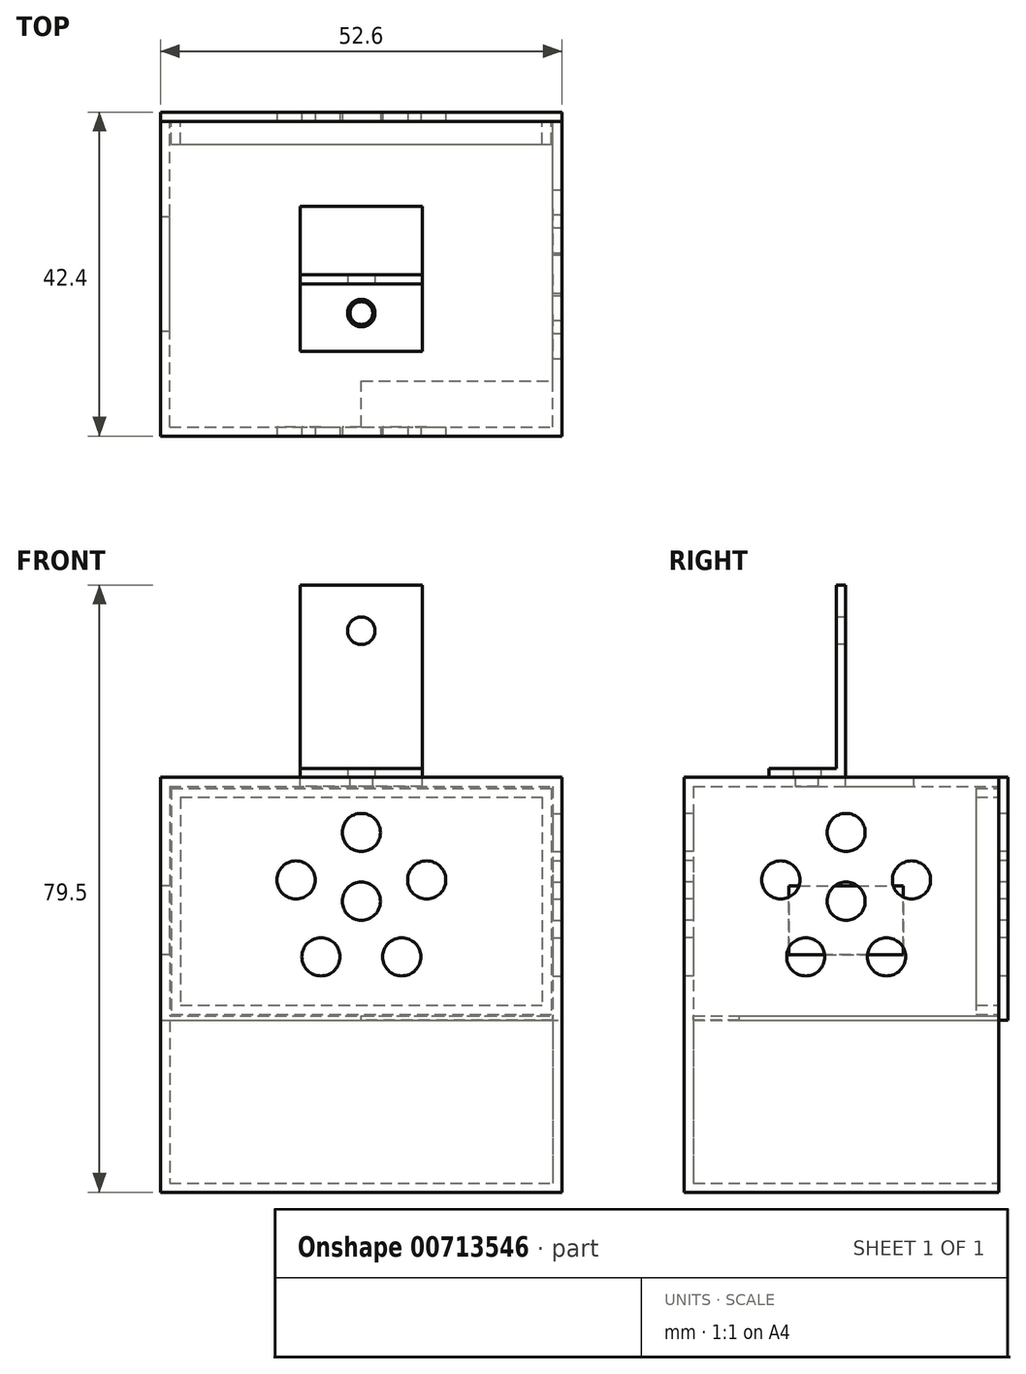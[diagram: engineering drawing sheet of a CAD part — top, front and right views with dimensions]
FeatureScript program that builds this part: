
annotation { "Feature Type Name" : "Feature", "Feature Type Description" : "" }
export const myFeature = defineFeature(function(context is Context, id is Id, definition is map)
    precondition{}
    {
        {
            var Q0;
            Q0=qCreatedBy(makeId("Top.planeOp"),FACE);
            var sketch = newSketch(context, id + "F0", { "sketchPlane" : qUnion([Q0])});
            skLineSegment(sketch, "E0.bottom", {"start": v(0, 0) * mm, "end": v(50.2, 0) * mm});
            skLineSegment(sketch, "E0.top", {"start": v(0, 40) * mm, "end": v(50.2, 40) * mm});
            skLineSegment(sketch, "E0.left", {"start": v(0, 0) * mm, "end": v(0, 40) * mm});
            skLineSegment(sketch, "E0.right", {"start": v(50.2, 0) * mm, "end": v(50.2, 40) * mm});
            skLineSegment(sketch, "E1.0", {"start": v(-1.2, -1.2) * mm, "end": v(-1.2, 40) * mm});
            skLineSegment(sketch, "E1.1", {"start": v(-1.2, -1.2) * mm, "end": v(51.4, -1.2) * mm});
            skLineSegment(sketch, "E1.2", {"start": v(51.4, -1.2) * mm, "end": v(51.4, 40) * mm});
            skLineSegment(sketch, "E2", {"start": v(-1.2, 40) * mm, "end": v(0, 40) * mm});
            skLineSegment(sketch, "E3", {"start": v(51.4, 40) * mm, "end": v(50.2, 40) * mm});
            skSolve(sketch);
        }
        {
            var Q0;
            Q0=makeQuery(id+"F0.imprint","IMPRINT",FACE,{"disambiguationData":[TD([[makeQuery(id+"F0.imprint","IMPRINT",EDGE,{"derivedFrom":sQuery(id+"F0.wireOp",EDGE,"E0.bottom")}),1.0]])]});
            extrude(context, id + "F1", {"entities" : qUnion([Q0]), "depth" : 1.2 * mm, "offsetDistance" : 25 * mm});
        }
        {
            var Q0;
            Q0=makeQuery(id+"F0.imprint","IMPRINT",FACE,{"disambiguationData":[TD([[makeQuery(id+"F0.imprint","IMPRINT",EDGE,{"derivedFrom":sQuery(id+"F0.wireOp",EDGE,"E0.bottom")}),-1.0]])]});
            extrude(context, id + "F2", {"entities" : qUnion([Q0]), "operationType" : NewBodyOperationType.ADD, "depth" : 22.5 * mm, "offsetDistance" : 25 * mm});
        }
        {
            var Q0;
            Q0=makeQuery(id+"F2.opExtrude","CAP_FACE",FACE,{"disambiguationData":[OSD([sQuery(id+"F0.wireOp",EDGE,"E0.bottom"),sQuery(id+"F0.wireOp",EDGE,"E0.left"),sQuery(id+"F0.wireOp",EDGE,"E0.right"),sQuery(id+"F0.wireOp",EDGE,"E1.0"),sQuery(id+"F0.wireOp",EDGE,"E1.1"),sQuery(id+"F0.wireOp",EDGE,"E1.2"),sQuery(id+"F0.wireOp",EDGE,"E2"),sQuery(id+"F0.wireOp",EDGE,"E3")])],"isStart":false});
            var sketch = newSketch(context, id + "F3", { "sketchPlane" : qUnion([Q0])});
            skLineSegment(sketch, "E4.0", {"start": v(0, 0) * mm, "end": v(0, 40) * mm});
            skLineSegment(sketch, "E4.1", {"start": v(-1.2, -1.2) * mm, "end": v(-1.2, 40) * mm});
            skLineSegment(sketch, "E4.2", {"start": v(-1.2, 40) * mm, "end": v(0, 40) * mm});
            skLineSegment(sketch, "E4.3", {"start": v(-1.2, -1.2) * mm, "end": v(51.4, -1.2) * mm});
            skLineSegment(sketch, "E4.4", {"start": v(51.4, -1.2) * mm, "end": v(51.4, 40) * mm});
            skLineSegment(sketch, "E4.5", {"start": v(51.4, 40) * mm, "end": v(50.2, 40) * mm});
            skLineSegment(sketch, "E5.bottom", {"start": v(-1.2, 40) * mm, "end": v(51.4, 40) * mm});
            skLineSegment(sketch, "E5.left", {"start": v(-1.2, 40) * mm, "end": v(-1.2, -1.2) * mm});
            skLineSegment(sketch, "E5.right", {"start": v(51.4, 40) * mm, "end": v(51.4, -1.2) * mm});
            skSolve(sketch);
        }
        {
            var Q0;
            {var subQ0=sQuery(id+"F3.wireOp",EDGE,"E4.0");Q0=makeQuery(id+"F3.imprint","IMPRINT",FACE,{"disambiguationData":[TD([[makeQuery(id+"F3.imprint","IMPRINT",EDGE,{"derivedFrom":subQ0}),-1.0]])]});}
            var Q1;
            {var subQ3=sQuery(id+"F3.wireOp",EDGE,"E4.0");Q1=makeQuery(id+"F3.imprint","IMPRINT",FACE,{"disambiguationData":[TD([[makeQuery(id+"F3.imprint","IMPRINT",EDGE,{"derivedFrom":subQ3}),1.0]])]});}
            extrude(context, id + "F4", {"entities" : qUnion([Q0, Q1]), "operationType" : NewBodyOperationType.ADD, "depth" : 0.6 * mm, "offsetDistance" : 25 * mm});
        }
        {
            var Q0;
            Q0=makeQuery(id+"F4.opExtrude","CAP_FACE",FACE,{"disambiguationData":[OSD([sQuery(id+"F3.wireOp",EDGE,"E5.bottom"),sQuery(id+"F3.wireOp",EDGE,"E4.3"),sQuery(id+"F3.wireOp",EDGE,"E5.left"),sQuery(id+"F3.wireOp",EDGE,"E5.right")])],"isStart":false});
            var sketch = newSketch(context, id + "F5", { "sketchPlane" : qUnion([Q0])});
            skLineSegment(sketch, "E6.0", {"start": v(-1.2, -1.2) * mm, "end": v(51.4, -1.2) * mm});
            skLineSegment(sketch, "E6.1", {"start": v(51.4, -1.2) * mm, "end": v(51.4, 40) * mm});
            skLineSegment(sketch, "E6.2", {"start": v(-1.2, -1.2) * mm, "end": v(-1.2, 40) * mm});
            skLineSegment(sketch, "E6.3", {"start": v(-1.2, 40) * mm, "end": v(51.4, 40) * mm});
            skLineSegment(sketch, "E7.0", {"start": v(0, 0) * mm, "end": v(50.2, 0) * mm});
            skLineSegment(sketch, "E7.1", {"start": v(50.2, 0) * mm, "end": v(50.2, 40) * mm});
            skLineSegment(sketch, "E7.2", {"start": v(0, 0) * mm, "end": v(0, 40) * mm});
            skPoint(sketch, "E8", {"position": v(25.1, 0) * mm});
            skLineSegment(sketch, "E9", {"start": v(25.1, 0) * mm, "end": v(25.1, 6) * mm});
            skLineSegment(sketch, "E10", {"start": v(25.1, 6) * mm, "end": v(50.2, 6) * mm});
            skSolve(sketch);
        }
        {
            var Q0;
            {var subQ3=sQuery(id+"F5.wireOp",EDGE,"E9");Q0=makeQuery(id+"F5.imprint","IMPRINT",FACE,{"disambiguationData":[TD([[makeQuery(id+"F5.imprint","IMPRINT",EDGE,{"derivedFrom":subQ3}),-1.0]])]});}
            extrude(context, id + "F6", {"entities" : qUnion([Q0]), "operationType" : NewBodyOperationType.REMOVE, "endBound" : BoundingType.UP_TO_NEXT, "oppositeDirection" : true, "depth" : 25 * mm, "offsetDistance" : 25 * mm});
        }
        {
            var Q0;
            Q0=makeQuery(id+"F4.opExtrude","CAP_FACE",FACE,{"disambiguationData":[OSD([sQuery(id+"F3.wireOp",EDGE,"E5.bottom"),sQuery(id+"F3.wireOp",EDGE,"E4.3"),sQuery(id+"F3.wireOp",EDGE,"E5.left"),sQuery(id+"F3.wireOp",EDGE,"E5.right")])],"isStart":false});
            var sketch = newSketch(context, id + "F7", { "sketchPlane" : qUnion([Q0])});
            skLineSegment(sketch, "E11.0", {"start": v(-1.2, -1.2) * mm, "end": v(-1.2, 40) * mm});
            skLineSegment(sketch, "E11.1", {"start": v(0, 0) * mm, "end": v(0, 40) * mm});
            skLineSegment(sketch, "E11.2", {"start": v(-1.2, -1.2) * mm, "end": v(51.4, -1.2) * mm});
            skLineSegment(sketch, "E11.3", {"start": v(0, 0) * mm, "end": v(50.2, 0) * mm});
            skLineSegment(sketch, "E11.4", {"start": v(50.2, 0) * mm, "end": v(50.2, 40) * mm});
            skSolve(sketch);
        }
        {
            var Q0;
            {var subQ3=sQuery(id+"F7.wireOp",EDGE,"E11.0");Q0=makeQuery(id+"F7.imprint","IMPRINT",FACE,{"disambiguationData":[TD([[makeQuery(id+"F7.imprint","IMPRINT",EDGE,{"derivedFrom":subQ3}),-1.0]])]});}
            extrude(context, id + "F8", {"entities" : qUnion([Q0]), "operationType" : NewBodyOperationType.ADD, "depth" : 30 * mm, "offsetDistance" : 25 * mm});
        }
        {
            var Q0;
            Q0=makeQuery(id+"F8.opExtrude","CAP_FACE",FACE,{"disambiguationData":[OSD([sQuery(id+"F3.wireOp",EDGE,"E5.bottom"),sQuery(id+"F3.wireOp",EDGE,"E5.right"),sQuery(id+"F7.wireOp",EDGE,"E11.0"),sQuery(id+"F7.wireOp",EDGE,"E11.1"),sQuery(id+"F7.wireOp",EDGE,"E11.2"),sQuery(id+"F7.wireOp",EDGE,"E11.3"),sQuery(id+"F7.wireOp",EDGE,"E11.4")])],"isStart":false});
            var sketch = newSketch(context, id + "F9", { "sketchPlane" : qUnion([Q0])});
            skLineSegment(sketch, "E12.0", {"start": v(51.4, -1.2) * mm, "end": v(51.4, 40) * mm});
            skLineSegment(sketch, "E12.1", {"start": v(50.2, 0) * mm, "end": v(50.2, 40) * mm});
            skLineSegment(sketch, "E12.2", {"start": v(0, 0) * mm, "end": v(50.2, 0) * mm});
            skLineSegment(sketch, "E12.3", {"start": v(-1.2, -1.2) * mm, "end": v(51.4, -1.2) * mm});
            skLineSegment(sketch, "E12.4", {"start": v(-1.2, -1.2) * mm, "end": v(-1.2, 40) * mm});
            skLineSegment(sketch, "E12.5", {"start": v(0, 0) * mm, "end": v(0, 40) * mm});
            skLineSegment(sketch, "E12.6", {"start": v(-1.2, 40) * mm, "end": v(0, 40) * mm});
            skLineSegment(sketch, "E12.7", {"start": v(50.2, 40) * mm, "end": v(51.4, 40) * mm});
            skLineSegment(sketch, "E13.bottom", {"start": v(-1.2, 40) * mm, "end": v(51.4, 40) * mm});
            skLineSegment(sketch, "E13.left", {"start": v(-1.2, 40) * mm, "end": v(-1.2, -1.2) * mm});
            skLineSegment(sketch, "E13.right", {"start": v(51.4, 40) * mm, "end": v(51.4, -1.2) * mm});
            skSolve(sketch);
        }
        {
            var Q0;
            {var subQ0=sQuery(id+"F9.wireOp",EDGE,"E12.1");Q0=makeQuery(id+"F9.imprint","IMPRINT",FACE,{"disambiguationData":[TD([[makeQuery(id+"F9.imprint","IMPRINT",EDGE,{"derivedFrom":subQ0}),1.0]])]});}
            var Q1;
            {var subQ3=sQuery(id+"F9.wireOp",EDGE,"E12.1");Q1=makeQuery(id+"F9.imprint","IMPRINT",FACE,{"disambiguationData":[TD([[makeQuery(id+"F9.imprint","IMPRINT",EDGE,{"derivedFrom":subQ3}),-1.0]])]});}
            extrude(context, id + "F10", {"entities" : qUnion([Q0, Q1]), "operationType" : NewBodyOperationType.ADD, "depth" : 1.2 * mm, "offsetDistance" : 25 * mm});
        }
        {
            var Q0;
            Q0=makeQuery(id+"F10.opExtrude","CAP_FACE",FACE,{"disambiguationData":[OSD([sQuery(id+"F9.wireOp",EDGE,"E13.bottom"),sQuery(id+"F9.wireOp",EDGE,"E12.3"),sQuery(id+"F9.wireOp",EDGE,"E13.left"),sQuery(id+"F9.wireOp",EDGE,"E13.right")])],"isStart":false});
            var sketch = newSketch(context, id + "F11", { "sketchPlane" : qUnion([Q0])});
            skLineSegment(sketch, "E14.bottom", {"start": v(17.1, 28.9) * mm, "end": v(33.1, 28.9) * mm});
            skLineSegment(sketch, "E14.top", {"start": v(17.1, 19.9) * mm, "end": v(33.1, 19.9) * mm});
            skLineSegment(sketch, "E14.left", {"start": v(17.1, 28.9) * mm, "end": v(17.1, 19.9) * mm});
            skLineSegment(sketch, "E14.right", {"start": v(33.1, 28.9) * mm, "end": v(33.1, 19.9) * mm});
            skLineSegment(sketch, "E15.0", {"start": v(51.4, -1.2) * mm, "end": v(51.4, 40) * mm});
            skLineSegment(sketch, "E15.1", {"start": v(-1.2, -1.2) * mm, "end": v(-1.2, 40) * mm});
            skLineSegment(sketch, "E15.2", {"start": v(-1.2, -1.2) * mm, "end": v(51.4, -1.2) * mm});
            skLineSegment(sketch, "E15.3", {"start": v(-1.2, 40) * mm, "end": v(51.4, 40) * mm});
            skPoint(sketch, "E16", {"position": v(25.1, 19.9) * mm});
            skCircle(sketch, "E17", {"center": v(25.1, 14.9) * mm, "radius": 1.5 * mm});
            skSolve(sketch);
        }
        {
            var Q0;
            Q0=makeQuery(id+"F11.imprint","IMPRINT",FACE,{"disambiguationData":[TD([[makeQuery(id+"F11.imprint","IMPRINT",EDGE,{"derivedFrom":sQuery(id+"F11.wireOp",EDGE,"E14.bottom")}),-1.0]])]});
            var Q1;
            Q1=makeQuery(id+"F11.imprint","IMPRINT",FACE,{"disambiguationData":[TD([[makeQuery(id+"F11.imprint","IMPRINT",EDGE,{"derivedFrom":sQuery(id+"F11.wireOp",EDGE,"E17")}),1.0]])]});
            extrude(context, id + "F12", {"entities" : qUnion([Q0, Q1]), "operationType" : NewBodyOperationType.REMOVE, "endBound" : BoundingType.UP_TO_NEXT, "oppositeDirection" : true, "depth" : 25 * mm, "offsetDistance" : 25 * mm});
        }
        {
            var Q0;
            Q0=makeQuery(id+"F10.boolean.opBoolean","MERGE",FACE,{"derivedFrom":[makeQuery(id+"F8.boolean.opBoolean","MERGE",FACE,{"derivedFrom":[makeQuery(id+"F4.boolean.opBoolean","MERGE",FACE,{"derivedFrom":[makeQuery(id+"F2.opExtrude","SWEPT_FACE",FACE,{"disambiguationData":[OSD([sQuery(id+"F0.wireOp",EDGE,"E1.0")])]}),makeQuery(id+"F4.opExtrude","SWEPT_FACE",FACE,{"disambiguationData":[OSD([sQuery(id+"F3.wireOp",EDGE,"E5.left")])]})]}),makeQuery(id+"F8.opExtrude","SWEPT_FACE",FACE,{"disambiguationData":[OSD([sQuery(id+"F7.wireOp",EDGE,"E11.0")])]})]}),makeQuery(id+"F10.opExtrude","SWEPT_FACE",FACE,{"disambiguationData":[OSD([sQuery(id+"F9.wireOp",EDGE,"E13.left")])]})]});
            var sketch = newSketch(context, id + "F13", { "sketchPlane" : qUnion([Q0])});
            skLineSegment(sketch, "E18.0", {"start": v(1.2, 54.3) * mm, "end": v(1.2, 0) * mm});
            skLineSegment(sketch, "E18.1", {"start": v(1.2, 54.3) * mm, "end": v(-40, 54.3) * mm});
            skLineSegment(sketch, "E18.2", {"start": v(-40, 54.3) * mm, "end": v(-40, 0) * mm});
            skLineSegment(sketch, "E18.3", {"start": v(1.2, 0) * mm, "end": v(-40, 0) * mm});
            skLineSegment(sketch, "E19.0", {"start": v(0, 23.1) * mm, "end": v(-40, 23.1) * mm});
            skLineSegment(sketch, "E20.1", {"start": v(0, 53.1) * mm, "end": v(-40, 53.1) * mm});
            skLineSegment(sketch, "E21.1", {"start": v(0, 53.1) * mm, "end": v(0, 23.1) * mm});
            skLineSegment(sketch, "E22.bottom", {"start": v(-27.5, 40.1) * mm, "end": v(-12.5, 40.1) * mm});
            skLineSegment(sketch, "E22.top", {"start": v(-27.5, 31.1) * mm, "end": v(-12.5, 31.1) * mm});
            skLineSegment(sketch, "E22.left", {"start": v(-27.5, 40.1) * mm, "end": v(-27.5, 31.1) * mm});
            skLineSegment(sketch, "E22.right", {"start": v(-12.5, 40.1) * mm, "end": v(-12.5, 31.1) * mm});
            skSolve(sketch);
        }
        {
            var Q0;
            Q0=makeQuery(id+"F13.imprint","IMPRINT",FACE,{"disambiguationData":[TD([[makeQuery(id+"F13.imprint","IMPRINT",EDGE,{"derivedFrom":sQuery(id+"F13.wireOp",EDGE,"E22.bottom")}),-1.0]])]});
            extrude(context, id + "F14", {"entities" : qUnion([Q0]), "operationType" : NewBodyOperationType.REMOVE, "endBound" : BoundingType.UP_TO_NEXT, "oppositeDirection" : true, "depth" : 25 * mm, "offsetDistance" : 25 * mm});
        }
        {
            var Q0;
            {var subQ0=sQuery(id+"F3.wireOp",EDGE,"E5.right");Q0=makeQuery(id+"F10.boolean.opBoolean","MERGE",FACE,{"derivedFrom":[makeQuery(id+"F8.boolean.opBoolean","MERGE",FACE,{"derivedFrom":[makeQuery(id+"F4.boolean.opBoolean","MERGE",FACE,{"derivedFrom":[makeQuery(id+"F2.opExtrude","SWEPT_FACE",FACE,{"disambiguationData":[OSD([sQuery(id+"F0.wireOp",EDGE,"E1.2")])]}),makeQuery(id+"F4.opExtrude","SWEPT_FACE",FACE,{"disambiguationData":[OSD([subQ0])]})]}),makeQuery(id+"F8.opExtrude","SWEPT_FACE",FACE,{"disambiguationData":[OSD([subQ0])]})]}),makeQuery(id+"F10.opExtrude","SWEPT_FACE",FACE,{"disambiguationData":[OSD([sQuery(id+"F9.wireOp",EDGE,"E13.right")])]})]});}
            var sketch = newSketch(context, id + "F15", { "sketchPlane" : qUnion([Q0])});
            skLineSegment(sketch, "E23.0", {"start": v(-1.2, 54.3) * mm, "end": v(40, 54.3) * mm});
            skLineSegment(sketch, "E23.1", {"start": v(40, 54.3) * mm, "end": v(40, 0) * mm});
            skLineSegment(sketch, "E23.2", {"start": v(-1.2, 54.3) * mm, "end": v(-1.2, 0) * mm});
            skLineSegment(sketch, "E23.3", {"start": v(-1.2, 0) * mm, "end": v(40, 0) * mm});
            skLineSegment(sketch, "E23.4", {"start": v(0, 53.1) * mm, "end": v(0, 1.2) * mm});
            skLineSegment(sketch, "E23.5", {"start": v(0, 53.1) * mm, "end": v(40, 53.1) * mm});
            skLineSegment(sketch, "E24.0", {"start": v(0, 1.2) * mm, "end": v(40, 1.2) * mm});
            skLineSegment(sketch, "E25.0", {"start": v(6, 23.1) * mm, "end": v(40, 23.1) * mm});
            skPoint(sketch, "E26", {"position": v(20, 53.1) * mm});
            skLineSegment(sketch, "E27", {"start": v(20, 53.1) * mm, "end": v(20, 23.1) * mm, "construction": true});
            skCircle(sketch, "E28", {"center": v(20, 38.1) * mm, "radius": 2.5 * mm});
            skCircle(sketch, "E29", {"center": v(20, 47.1) * mm, "radius": 2.5 * mm});
            skCircle(sketch, "E30.1.0", {"center": v(11.44, 40.88) * mm, "radius": 2.5 * mm});
            skCircle(sketch, "E30.2.0", {"center": v(14.7, 30.82) * mm, "radius": 2.5 * mm});
            skCircle(sketch, "E30.3.0", {"center": v(25.3, 30.82) * mm, "radius": 2.5 * mm});
            skCircle(sketch, "E30.4.0", {"center": v(28.56, 40.88) * mm, "radius": 2.5 * mm});
            skSolve(sketch);
        }
        {
            var Q0;
            Q0=makeQuery(id+"F15.imprint","IMPRINT",FACE,{"disambiguationData":[TD([[makeQuery(id+"F15.imprint","IMPRINT",EDGE,{"derivedFrom":sQuery(id+"F15.wireOp",EDGE,"E30.4.0")}),1.0]])]});
            var Q1;
            Q1=makeQuery(id+"F15.imprint","IMPRINT",FACE,{"disambiguationData":[TD([[makeQuery(id+"F15.imprint","IMPRINT",EDGE,{"derivedFrom":sQuery(id+"F15.wireOp",EDGE,"E29")}),1.0]])]});
            var Q2;
            Q2=makeQuery(id+"F15.imprint","IMPRINT",FACE,{"disambiguationData":[TD([[makeQuery(id+"F15.imprint","IMPRINT",EDGE,{"derivedFrom":sQuery(id+"F15.wireOp",EDGE,"E28")}),1.0]])]});
            var Q3;
            Q3=makeQuery(id+"F15.imprint","IMPRINT",FACE,{"disambiguationData":[TD([[makeQuery(id+"F15.imprint","IMPRINT",EDGE,{"derivedFrom":sQuery(id+"F15.wireOp",EDGE,"E30.1.0")}),1.0]])]});
            var Q4;
            Q4=makeQuery(id+"F15.imprint","IMPRINT",FACE,{"disambiguationData":[TD([[makeQuery(id+"F15.imprint","IMPRINT",EDGE,{"derivedFrom":sQuery(id+"F15.wireOp",EDGE,"E30.2.0")}),1.0]])]});
            var Q5;
            Q5=makeQuery(id+"F15.imprint","IMPRINT",FACE,{"disambiguationData":[TD([[makeQuery(id+"F15.imprint","IMPRINT",EDGE,{"derivedFrom":sQuery(id+"F15.wireOp",EDGE,"E30.3.0")}),1.0]])]});
            extrude(context, id + "F16", {"entities" : qUnion([Q0, Q1, Q2, Q3, Q4, Q5]), "operationType" : NewBodyOperationType.REMOVE, "endBound" : BoundingType.UP_TO_NEXT, "oppositeDirection" : true, "depth" : 25 * mm, "offsetDistance" : 25 * mm});
        }
        {
            var Q0;
            Q0=makeQuery(id+"F10.boolean.opBoolean","MERGE",FACE,{"derivedFrom":[makeQuery(id+"F8.boolean.opBoolean","MERGE",FACE,{"derivedFrom":[makeQuery(id+"F4.boolean.opBoolean","MERGE",FACE,{"derivedFrom":[makeQuery(id+"F2.opExtrude","SWEPT_FACE",FACE,{"disambiguationData":[OSD([sQuery(id+"F0.wireOp",EDGE,"E1.1")])]}),makeQuery(id+"F4.opExtrude","SWEPT_FACE",FACE,{"disambiguationData":[OSD([sQuery(id+"F3.wireOp",EDGE,"E4.3")])]})]}),makeQuery(id+"F8.opExtrude","SWEPT_FACE",FACE,{"disambiguationData":[OSD([sQuery(id+"F7.wireOp",EDGE,"E11.2")])]})]}),makeQuery(id+"F10.opExtrude","SWEPT_FACE",FACE,{"disambiguationData":[OSD([sQuery(id+"F9.wireOp",EDGE,"E12.3")])]})]});
            var sketch = newSketch(context, id + "F17", { "sketchPlane" : qUnion([Q0])});
            skLineSegment(sketch, "E31.0", {"start": v(51.4, 54.3) * mm, "end": v(51.4, 0) * mm});
            skLineSegment(sketch, "E31.1", {"start": v(-1.2, 54.3) * mm, "end": v(51.4, 54.3) * mm});
            skLineSegment(sketch, "E31.2", {"start": v(-1.2, 54.3) * mm, "end": v(-1.2, 0) * mm});
            skLineSegment(sketch, "E31.3", {"start": v(-1.2, 0) * mm, "end": v(51.4, 0) * mm});
            skLineSegment(sketch, "E32.0", {"start": v(0, 53.1) * mm, "end": v(50.2, 53.1) * mm});
            skLineSegment(sketch, "E32.1", {"start": v(0, 53.1) * mm, "end": v(0, 23.1) * mm});
            skLineSegment(sketch, "E32.2", {"start": v(50.2, 53.1) * mm, "end": v(50.2, 1.2) * mm});
            skLineSegment(sketch, "E32.3", {"start": v(0, 23.1) * mm, "end": v(25.1, 23.1) * mm});
            skPoint(sketch, "E33", {"position": v(25.1, 53.1) * mm});
            skLineSegment(sketch, "E34", {"start": v(25.1, 53.1) * mm, "end": v(25.1, 23.1) * mm, "construction": true});
            skPoint(sketch, "E35", {"position": v(25.1, 38.1) * mm});
            skCircle(sketch, "E36", {"center": v(25.1, 38.1) * mm, "radius": 2.5 * mm});
            skCircle(sketch, "E37", {"center": v(25.1, 47.1) * mm, "radius": 2.5 * mm});
            skCircle(sketch, "E38.1.0", {"center": v(16.54, 40.88) * mm, "radius": 2.5 * mm});
            skCircle(sketch, "E38.2.0", {"center": v(19.8, 30.82) * mm, "radius": 2.5 * mm});
            skCircle(sketch, "E38.3.0", {"center": v(30.4, 30.82) * mm, "radius": 2.5 * mm});
            skCircle(sketch, "E38.4.0", {"center": v(33.66, 40.88) * mm, "radius": 2.5 * mm});
            skSolve(sketch);
        }
        {
            var Q0;
            Q0=makeQuery(id+"F17.imprint","IMPRINT",FACE,{"disambiguationData":[TD([[makeQuery(id+"F17.imprint","IMPRINT",EDGE,{"derivedFrom":sQuery(id+"F17.wireOp",EDGE,"E37")}),1.0]])]});
            var Q1;
            Q1=makeQuery(id+"F17.imprint","IMPRINT",FACE,{"disambiguationData":[TD([[makeQuery(id+"F17.imprint","IMPRINT",EDGE,{"derivedFrom":sQuery(id+"F17.wireOp",EDGE,"E38.4.0")}),1.0]])]});
            var Q2;
            Q2=makeQuery(id+"F17.imprint","IMPRINT",FACE,{"disambiguationData":[TD([[makeQuery(id+"F17.imprint","IMPRINT",EDGE,{"derivedFrom":sQuery(id+"F17.wireOp",EDGE,"E38.3.0")}),1.0]])]});
            var Q3;
            Q3=makeQuery(id+"F17.imprint","IMPRINT",FACE,{"disambiguationData":[TD([[makeQuery(id+"F17.imprint","IMPRINT",EDGE,{"derivedFrom":sQuery(id+"F17.wireOp",EDGE,"E36")}),1.0]])]});
            var Q4;
            Q4=makeQuery(id+"F17.imprint","IMPRINT",FACE,{"disambiguationData":[TD([[makeQuery(id+"F17.imprint","IMPRINT",EDGE,{"derivedFrom":sQuery(id+"F17.wireOp",EDGE,"E38.1.0")}),1.0]])]});
            var Q5;
            Q5=makeQuery(id+"F17.imprint","IMPRINT",FACE,{"disambiguationData":[TD([[makeQuery(id+"F17.imprint","IMPRINT",EDGE,{"derivedFrom":sQuery(id+"F17.wireOp",EDGE,"E38.2.0")}),1.0]])]});
            extrude(context, id + "F18", {"entities" : qUnion([Q0, Q1, Q2, Q3, Q4, Q5]), "operationType" : NewBodyOperationType.REMOVE, "endBound" : BoundingType.UP_TO_NEXT, "oppositeDirection" : true, "depth" : 25 * mm, "offsetDistance" : 25 * mm});
        }
        {
            var Q0;
            Q0=makeQuery(id+"F10.opExtrude","CAP_FACE",FACE,{"disambiguationData":[OSD([sQuery(id+"F9.wireOp",EDGE,"E13.bottom"),sQuery(id+"F9.wireOp",EDGE,"E12.3"),sQuery(id+"F9.wireOp",EDGE,"E13.left"),sQuery(id+"F9.wireOp",EDGE,"E13.right")])],"isStart":false});
            var sketch = newSketch(context, id + "F19", { "sketchPlane" : qUnion([Q0])});
            skLineSegment(sketch, "E39.0", {"start": v(17.1, 19.9) * mm, "end": v(33.1, 19.9) * mm});
            skCircle(sketch, "E39.1", {"center": v(25.1, 14.9) * mm, "radius": 1.5 * mm});
            skLineSegment(sketch, "E39.2", {"start": v(17.1, 28.9) * mm, "end": v(17.1, 19.9) * mm});
            skLineSegment(sketch, "E39.3", {"start": v(33.1, 28.9) * mm, "end": v(33.1, 19.9) * mm});
            skLineSegment(sketch, "E40.top", {"start": v(17.1, 9.9) * mm, "end": v(33.1, 9.9) * mm});
            skLineSegment(sketch, "E40.left", {"start": v(17.1, 19.9) * mm, "end": v(17.1, 9.9) * mm});
            skLineSegment(sketch, "E40.right", {"start": v(33.1, 19.9) * mm, "end": v(33.1, 9.9) * mm});
            skCircle(sketch, "E41", {"center": v(25.1, 14.9) * mm, "radius": 1.8 * mm});
            skSolve(sketch);
        }
        {
            var Q0;
            Q0=makeQuery(id+"F19.imprint","IMPRINT",FACE,{"disambiguationData":[TD([[makeQuery(id+"F19.imprint","IMPRINT",EDGE,{"derivedFrom":sQuery(id+"F19.wireOp",EDGE,"E39.0")}),-1.0]])]});
            extrude(context, id + "F20", {"entities" : qUnion([Q0]), "depth" : 1.2 * mm, "offsetDistance" : 25 * mm});
        }
        {
            var Q0;
            Q0=makeQuery(id+"F20.opExtrude","CAP_FACE",FACE,{"disambiguationData":[OSD([sQuery(id+"F19.wireOp",EDGE,"E39.1"),sQuery(id+"F19.wireOp",EDGE,"E39.0"),sQuery(id+"F19.wireOp",EDGE,"E40.top"),sQuery(id+"F19.wireOp",EDGE,"E40.left"),sQuery(id+"F19.wireOp",EDGE,"E40.right")])],"isStart":false});
            var sketch = newSketch(context, id + "F21", { "sketchPlane" : qUnion([Q0])});
            skLineSegment(sketch, "E42.0", {"start": v(17.1, 19.9) * mm, "end": v(33.1, 19.9) * mm});
            skLineSegment(sketch, "E42.1", {"start": v(17.1, 19.9) * mm, "end": v(17.1, 9.9) * mm});
            skLineSegment(sketch, "E42.2", {"start": v(33.1, 19.9) * mm, "end": v(33.1, 9.9) * mm});
            skLineSegment(sketch, "E43.top", {"start": v(17.1, 18.7) * mm, "end": v(33.1, 18.7) * mm});
            skLineSegment(sketch, "E43.left", {"start": v(17.1, 19.9) * mm, "end": v(17.1, 18.7) * mm});
            skLineSegment(sketch, "E43.right", {"start": v(33.1, 19.9) * mm, "end": v(33.1, 18.7) * mm});
            skSolve(sketch);
        }
        {
            var Q0;
            Q0=makeQuery(id+"F21.imprint","IMPRINT",FACE,{"disambiguationData":[TD([[makeQuery(id+"F21.imprint","IMPRINT",EDGE,{"derivedFrom":sQuery(id+"F21.wireOp",EDGE,"E42.0")}),-1.0]])]});
            extrude(context, id + "F22", {"entities" : qUnion([Q0]), "operationType" : NewBodyOperationType.ADD, "depth" : 24 * mm, "offsetDistance" : 25 * mm});
        }
        {
            var Q0;
            Q0=makeQuery(id+"F22.opExtrude","SWEPT_FACE",FACE,{"disambiguationData":[OSD([sQuery(id+"F21.wireOp",EDGE,"E43.top")])]});
            var sketch = newSketch(context, id + "F23", { "sketchPlane" : qUnion([Q0])});
            skCircle(sketch, "E44", {"center": v(25.1, 73.5) * mm, "radius": 1.8 * mm});
            skPoint(sketch, "E44.centerSnap0", {"position": v(25.1, 79.5) * mm});
            skSolve(sketch);
        }
        {
            var Q0;
            Q0=makeQuery(id+"F23.imprint","IMPRINT",FACE,{"disambiguationData":[TD([[makeQuery(id+"F23.imprint","IMPRINT",EDGE,{"derivedFrom":sQuery(id+"F23.wireOp",EDGE,"E44")}),1.0]])]});
            extrude(context, id + "F24", {"entities" : qUnion([Q0]), "operationType" : NewBodyOperationType.REMOVE, "endBound" : BoundingType.UP_TO_NEXT, "oppositeDirection" : true, "depth" : 25 * mm, "offsetDistance" : 25 * mm});
        }
        {
            var Q0;
            {var subQ0=sQuery(id+"F3.wireOp",EDGE,"E5.bottom");var subQ1=makeQuery(id+"F4.opExtrude","CAP_EDGE",EDGE,{"disambiguationData":[OSD([subQ0])],"isStart":false});Q0=makeQuery(id+"F10.boolean.opBoolean","MERGE",FACE,{"derivedFrom":[makeQuery(id+"F8.boolean.opBoolean","MERGE",FACE,{"derivedFrom":[makeQuery(id+"F4.boolean.opBoolean","MERGE",FACE,{"derivedFrom":[makeQuery(id+"F2.boolean.opBoolean","MERGE",FACE,{"derivedFrom":[makeQuery(id+"F1.opExtrude","SWEPT_FACE",FACE,{"disambiguationData":[OSD([sQuery(id+"F0.wireOp",EDGE,"E0.top")])]}),makeQuery(id+"F2.opExtrude","SWEPT_FACE",FACE,{"disambiguationData":[OSD([sQuery(id+"F0.wireOp",EDGE,"E2")])]}),makeQuery(id+"F2.opExtrude","SWEPT_FACE",FACE,{"disambiguationData":[OSD([sQuery(id+"F0.wireOp",EDGE,"E3")])]})]}),makeQuery(id+"F4.opExtrude","SWEPT_FACE",FACE,{"disambiguationData":[OSD([subQ0])]})]}),makeQuery(id+"F8.opExtrude","SWEPT_FACE",FACE,{"disambiguationData":[OSD([subQ0]),TDD([makeQuery(id+"F7.imprint","IMPRINT",EDGE,{"disambiguationData":[TD([[makeQuery(id+"F7.imprint","INTERSECT",VERTEX,{"derivedFrom":[subQ1,sQuery(id+"F7.wireOp",EDGE,"E11.0")]}),-1.0]])],"derivedFrom":subQ1})])]}),makeQuery(id+"F8.opExtrude","SWEPT_FACE",FACE,{"disambiguationData":[OSD([subQ0]),TDD([makeQuery(id+"F7.imprint","IMPRINT",EDGE,{"disambiguationData":[TD([[makeQuery(id+"F7.imprint","INTERSECT",VERTEX,{"derivedFrom":[subQ1,makeQuery(id+"F4.opExtrude","CAP_EDGE",EDGE,{"disambiguationData":[OSD([sQuery(id+"F3.wireOp",EDGE,"E5.right")])],"isStart":false})]}),1.0]])],"derivedFrom":subQ1})])]})]}),makeQuery(id+"F10.opExtrude","SWEPT_FACE",FACE,{"disambiguationData":[OSD([sQuery(id+"F9.wireOp",EDGE,"E13.bottom")])]})]});}
            var sketch = newSketch(context, id + "F25", { "sketchPlane" : qUnion([Q0])});
            skLineSegment(sketch, "E45.0", {"start": v(0, 53.1) * mm, "end": v(-50.2, 53.1) * mm});
            skLineSegment(sketch, "E45.1", {"start": v(-50.2, 53.1) * mm, "end": v(-50.2, 23.1) * mm});
            skLineSegment(sketch, "E45.2", {"start": v(0, 23.1) * mm, "end": v(-50.2, 23.1) * mm});
            skLineSegment(sketch, "E45.3", {"start": v(0, 53.1) * mm, "end": v(0, 23.1) * mm});
            skLineSegment(sketch, "E45.4", {"start": v(1.2, 54.3) * mm, "end": v(1.2, 0) * mm});
            skLineSegment(sketch, "E45.5", {"start": v(0, 22.5) * mm, "end": v(-50.2, 22.5) * mm});
            skLineSegment(sketch, "E45.6", {"start": v(1.2, 54.3) * mm, "end": v(-51.4, 54.3) * mm});
            skLineSegment(sketch, "E45.7", {"start": v(-51.4, 54.3) * mm, "end": v(-51.4, 0) * mm});
            skLineSegment(sketch, "E45.8", {"start": v(-50.2, 22.5) * mm, "end": v(-50.2, 1.2) * mm});
            skLineSegment(sketch, "E46.bottom", {"start": v(-51.4, 54.3) * mm, "end": v(1.2, 54.3) * mm});
            skLineSegment(sketch, "E46.top", {"start": v(-51.4, 22.5) * mm, "end": v(1.2, 22.5) * mm});
            skLineSegment(sketch, "E46.left", {"start": v(-51.4, 54.3) * mm, "end": v(-51.4, 22.5) * mm});
            skLineSegment(sketch, "E46.right", {"start": v(1.2, 54.3) * mm, "end": v(1.2, 22.5) * mm});
            skCircle(sketch, "E47.0", {"center": v(-25.1, 47.1) * mm, "radius": 2.5 * mm});
            skCircle(sketch, "E47.1", {"center": v(-16.54, 40.88) * mm, "radius": 2.5 * mm});
            skCircle(sketch, "E47.2", {"center": v(-25.1, 38.1) * mm, "radius": 2.5 * mm});
            skCircle(sketch, "E47.3", {"center": v(-19.8, 30.82) * mm, "radius": 2.5 * mm});
            skCircle(sketch, "E47.4", {"center": v(-30.4, 30.82) * mm, "radius": 2.5 * mm});
            skCircle(sketch, "E47.5", {"center": v(-33.66, 40.88) * mm, "radius": 2.5 * mm});
            skSolve(sketch);
        }
        {
            var Q0;
            Q0=makeQuery(id+"F25.imprint","IMPRINT",FACE,{"disambiguationData":[TD([[makeQuery(id+"F25.imprint","IMPRINT",EDGE,{"derivedFrom":sQuery(id+"F25.wireOp",EDGE,"E45.0")}),1.0]])]});
            var Q1;
            Q1=makeQuery(id+"F25.imprint","IMPRINT",FACE,{"disambiguationData":[TD([[makeQuery(id+"F25.imprint","IMPRINT",EDGE,{"derivedFrom":sQuery(id+"F25.wireOp",EDGE,"E45.0")}),-1.0]])]});
            extrude(context, id + "F26", {"entities" : qUnion([Q0, Q1]), "depth" : 1.2 * mm, "offsetDistance" : 25 * mm});
        }
        {
            var Q0;
            Q0=makeQuery(id+"F26.opExtrude","CAP_FACE",FACE,{"disambiguationData":[OSD([sQuery(id+"F25.wireOp",EDGE,"E46.bottom"),sQuery(id+"F25.wireOp",EDGE,"E46.top"),sQuery(id+"F25.wireOp",EDGE,"E46.left"),sQuery(id+"F25.wireOp",EDGE,"E46.right"),sQuery(id+"F25.wireOp",EDGE,"E47.0"),sQuery(id+"F25.wireOp",EDGE,"E47.1"),sQuery(id+"F25.wireOp",EDGE,"E47.2"),sQuery(id+"F25.wireOp",EDGE,"E47.3"),sQuery(id+"F25.wireOp",EDGE,"E47.4"),sQuery(id+"F25.wireOp",EDGE,"E47.5")])],"isStart":true});
            var sketch = newSketch(context, id + "F27", { "sketchPlane" : qUnion([Q0])});
            skLineSegment(sketch, "E48.0", {"start": v(50.2, 53.1) * mm, "end": v(50.2, 23.1) * mm});
            skLineSegment(sketch, "E48.1", {"start": v(0, 23.1) * mm, "end": v(50.2, 23.1) * mm});
            skLineSegment(sketch, "E48.2", {"start": v(0, 53.1) * mm, "end": v(50.2, 53.1) * mm});
            skLineSegment(sketch, "E48.3", {"start": v(0, 53.1) * mm, "end": v(0, 23.1) * mm});
            skLineSegment(sketch, "E49.0", {"start": v(0.2, 52.9) * mm, "end": v(50, 52.9) * mm});
            skLineSegment(sketch, "E49.1", {"start": v(0.2, 52.9) * mm, "end": v(0.2, 23.3) * mm});
            skLineSegment(sketch, "E49.2", {"start": v(0.2, 23.3) * mm, "end": v(50, 23.3) * mm});
            skLineSegment(sketch, "E49.3", {"start": v(50, 52.9) * mm, "end": v(50, 23.3) * mm});
            skLineSegment(sketch, "E50.0", {"start": v(1.4, 51.7) * mm, "end": v(48.8, 51.7) * mm});
            skLineSegment(sketch, "E50.1", {"start": v(1.4, 51.7) * mm, "end": v(1.4, 24.5) * mm});
            skLineSegment(sketch, "E50.2", {"start": v(1.4, 24.5) * mm, "end": v(48.8, 24.5) * mm});
            skLineSegment(sketch, "E50.3", {"start": v(48.8, 51.7) * mm, "end": v(48.8, 24.5) * mm});
            skLineSegment(sketch, "E51.bottom", {"start": v(48.8, 53.1) * mm, "end": v(50.2, 53.1) * mm});
            skLineSegment(sketch, "E51.top", {"start": v(48.8, 51.7) * mm, "end": v(50.2, 51.7) * mm});
            skLineSegment(sketch, "E51.left", {"start": v(48.8, 53.1) * mm, "end": v(48.8, 51.7) * mm});
            skLineSegment(sketch, "E51.right", {"start": v(50.2, 53.1) * mm, "end": v(50.2, 51.7) * mm});
            skLineSegment(sketch, "E52.bottom", {"start": v(50.2, 24.5) * mm, "end": v(48.8, 24.5) * mm});
            skLineSegment(sketch, "E52.top", {"start": v(50.2, 23.1) * mm, "end": v(48.8, 23.1) * mm});
            skLineSegment(sketch, "E52.left", {"start": v(50.2, 24.5) * mm, "end": v(50.2, 23.1) * mm});
            skLineSegment(sketch, "E52.right", {"start": v(48.8, 24.5) * mm, "end": v(48.8, 23.1) * mm});
            skLineSegment(sketch, "E53.bottom", {"start": v(1.4, 53.1) * mm, "end": v(0, 53.1) * mm});
            skLineSegment(sketch, "E53.top", {"start": v(1.4, 51.7) * mm, "end": v(0, 51.7) * mm});
            skLineSegment(sketch, "E53.left", {"start": v(1.4, 53.1) * mm, "end": v(1.4, 51.7) * mm});
            skLineSegment(sketch, "E53.right", {"start": v(0, 53.1) * mm, "end": v(0, 51.7) * mm});
            skLineSegment(sketch, "E54.bottom", {"start": v(0, 24.5) * mm, "end": v(1.4, 24.5) * mm});
            skLineSegment(sketch, "E54.top", {"start": v(0, 23.1) * mm, "end": v(1.4, 23.1) * mm});
            skLineSegment(sketch, "E54.left", {"start": v(0, 24.5) * mm, "end": v(0, 23.1) * mm});
            skLineSegment(sketch, "E54.right", {"start": v(1.4, 24.5) * mm, "end": v(1.4, 23.1) * mm});
            skSolve(sketch);
        }
        {
            var Q0;
            {var subQ0=sQuery(id+"F27.wireOp",EDGE,"E49.3");var subQ1=sQuery(id+"F27.wireOp",EDGE,"E49.0");var subQ2=makeQuery(id+"F27.imprint","INTERSECT",VERTEX,{"derivedFrom":[subQ1,subQ0]});Q0=makeQuery(id+"F27.imprint","IMPRINT",FACE,{"disambiguationData":[TD([[makeQuery(id+"F27.imprint","IMPRINT",EDGE,{"disambiguationData":[TD([[subQ2,1.0]])],"derivedFrom":subQ1}),-1.0]])]});}
            var Q1;
            {var subQ5=sQuery(id+"F27.wireOp",EDGE,"E50.0");Q1=makeQuery(id+"F27.imprint","IMPRINT",FACE,{"disambiguationData":[TD([[makeQuery(id+"F27.imprint","IMPRINT",EDGE,{"derivedFrom":subQ5}),1.0]])]});}
            var Q2;
            {var subQ0=sQuery(id+"F27.wireOp",EDGE,"E49.1");var subQ1=sQuery(id+"F27.wireOp",EDGE,"E49.0");var subQ2=makeQuery(id+"F27.imprint","INTERSECT",VERTEX,{"derivedFrom":[subQ1,subQ0]});Q2=makeQuery(id+"F27.imprint","IMPRINT",FACE,{"disambiguationData":[TD([[makeQuery(id+"F27.imprint","IMPRINT",EDGE,{"disambiguationData":[TD([[subQ2,-1.0]])],"derivedFrom":subQ1}),-1.0]])]});}
            var Q3;
            {var subQ0=sQuery(id+"F27.wireOp",EDGE,"E53.bottom");Q3=makeQuery(id+"F27.imprint","IMPRINT",FACE,{"disambiguationData":[TD([[makeQuery(id+"F27.imprint","IMPRINT",EDGE,{"derivedFrom":subQ0}),1.0]])]});}
            var Q4;
            {var subQ5=sQuery(id+"F27.wireOp",EDGE,"E50.1");Q4=makeQuery(id+"F27.imprint","IMPRINT",FACE,{"disambiguationData":[TD([[makeQuery(id+"F27.imprint","IMPRINT",EDGE,{"derivedFrom":subQ5}),-1.0]])]});}
            var Q5;
            {var subQ0=sQuery(id+"F27.wireOp",EDGE,"E49.2");var subQ1=sQuery(id+"F27.wireOp",EDGE,"E49.1");var subQ2=makeQuery(id+"F27.imprint","INTERSECT",VERTEX,{"derivedFrom":[subQ1,subQ0]});Q5=makeQuery(id+"F27.imprint","IMPRINT",FACE,{"disambiguationData":[TD([[makeQuery(id+"F27.imprint","IMPRINT",EDGE,{"disambiguationData":[TD([[subQ2,1.0]])],"derivedFrom":subQ1}),1.0]])]});}
            var Q6;
            {var subQ4=sQuery(id+"F27.wireOp",EDGE,"E54.top");Q6=makeQuery(id+"F27.imprint","IMPRINT",FACE,{"disambiguationData":[TD([[makeQuery(id+"F27.imprint","IMPRINT",EDGE,{"derivedFrom":subQ4}),1.0]])]});}
            var Q7;
            {var subQ5=sQuery(id+"F27.wireOp",EDGE,"E50.2");Q7=makeQuery(id+"F27.imprint","IMPRINT",FACE,{"disambiguationData":[TD([[makeQuery(id+"F27.imprint","IMPRINT",EDGE,{"derivedFrom":subQ5}),-1.0]])]});}
            var Q8;
            {var subQ0=sQuery(id+"F27.wireOp",EDGE,"E49.3");var subQ1=sQuery(id+"F27.wireOp",EDGE,"E49.2");var subQ2=makeQuery(id+"F27.imprint","INTERSECT",VERTEX,{"derivedFrom":[subQ1,subQ0]});Q8=makeQuery(id+"F27.imprint","IMPRINT",FACE,{"disambiguationData":[TD([[makeQuery(id+"F27.imprint","IMPRINT",EDGE,{"disambiguationData":[TD([[subQ2,1.0]])],"derivedFrom":subQ1}),1.0]])]});}
            var Q9;
            {var subQ0=sQuery(id+"F27.wireOp",EDGE,"E52.top");Q9=makeQuery(id+"F27.imprint","IMPRINT",FACE,{"disambiguationData":[TD([[makeQuery(id+"F27.imprint","IMPRINT",EDGE,{"derivedFrom":subQ0}),-1.0]])]});}
            var Q10;
            {var subQ5=sQuery(id+"F27.wireOp",EDGE,"E50.3");Q10=makeQuery(id+"F27.imprint","IMPRINT",FACE,{"disambiguationData":[TD([[makeQuery(id+"F27.imprint","IMPRINT",EDGE,{"derivedFrom":subQ5}),1.0]])]});}
            var Q11;
            {var subQ4=sQuery(id+"F27.wireOp",EDGE,"E51.bottom");Q11=makeQuery(id+"F27.imprint","IMPRINT",FACE,{"disambiguationData":[TD([[makeQuery(id+"F27.imprint","IMPRINT",EDGE,{"derivedFrom":subQ4}),-1.0]])]});}
            extrude(context, id + "F28", {"entities" : qUnion([Q0, Q1, Q2, Q3, Q4, Q5, Q6, Q7, Q8, Q9, Q10, Q11]), "operationType" : NewBodyOperationType.ADD, "depth" : 3 * mm, "offsetDistance" : 25 * mm});
        }
    });
